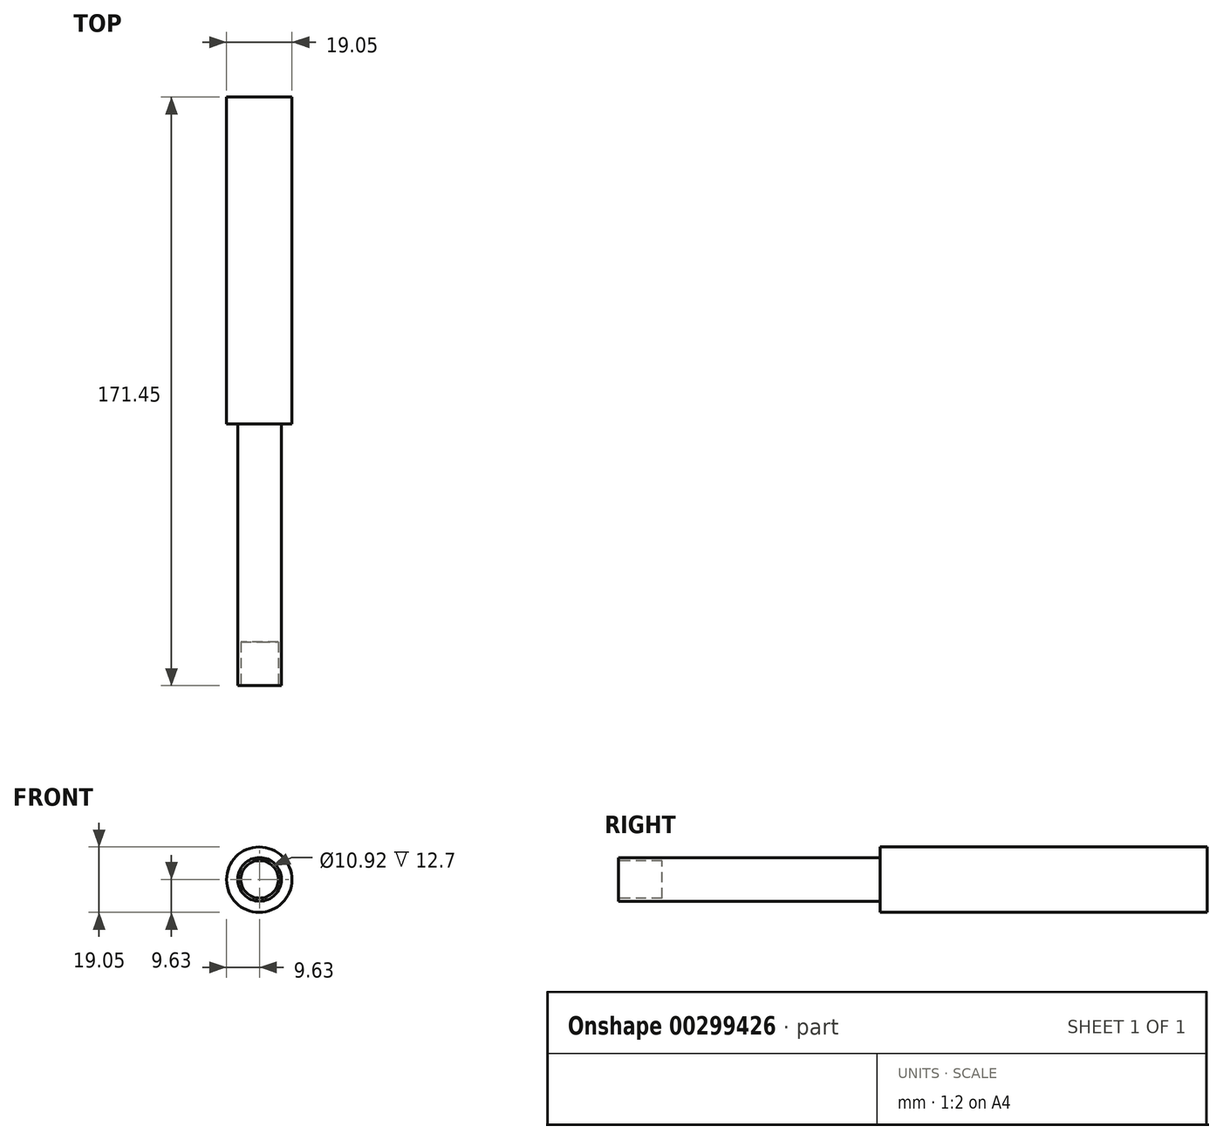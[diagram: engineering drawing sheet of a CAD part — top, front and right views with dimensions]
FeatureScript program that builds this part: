
annotation { "Feature Type Name" : "Feature", "Feature Type Description" : "" }
export const myFeature = defineFeature(function(context is Context, id is Id, definition is map)
    precondition{}
    {
        {
            var Q0;
            Q0=qCreatedBy(makeId("Front.planeOp"),FACE);
            var sketch = newSketch(context, id + "F0", { "sketchPlane" : qUnion([Q0])});
            skCircle(sketch, "E0", {"center": v(-0.1, -0.1) * mm, "radius": 9.53 * mm});
            skSolve(sketch);
        }
        {
            var Q0;
            Q0=makeQuery(id+"F0.imprint","IMPRINT",FACE,{"disambiguationData":[TD([[makeQuery(id+"F0.imprint","IMPRINT",EDGE,{"derivedFrom":sQuery(id+"F0.wireOp",EDGE,"E0")}),1.0]])]});
            extrude(context, id + "F1", {"entities" : qUnion([Q0]), "oppositeDirection" : true, "depth" : 95.25 * mm});
        }
        {
            var Q0;
            Q0=makeQuery(id+"F1.opExtrude","CAP_FACE",FACE,{"disambiguationData":[OSD([sQuery(id+"F0.wireOp",EDGE,"E0")])],"isStart":true});
            var sketch = newSketch(context, id + "F2", { "sketchPlane" : qUnion([Q0])});
            skCircle(sketch, "E1", {"center": v(0, 0) * mm, "radius": 6.35 * mm});
            skSolve(sketch);
        }
        {
            var Q0;
            Q0 = qSketchRegion(id + "F2", true);
            extrude(context, id + "F3", {"entities" : qUnion([Q0]), "operationType" : NewBodyOperationType.ADD, "depth" : 76.2 * mm});
        }
        {
            var Q0;
            Q0=makeQuery(id+"F3.opExtrude","CAP_FACE",FACE,{"disambiguationData":[OSD([sQuery(id+"F2.wireOp",EDGE,"E1")])],"isStart":false});
            var sketch = newSketch(context, id + "F4", { "sketchPlane" : qUnion([Q0])});
            skCircle(sketch, "E2", {"center": v(0, 0) * mm, "radius": 5.46 * mm});
            skSolve(sketch);
        }
        {
            var Q0;
            Q0=makeQuery(id+"F4.imprint","IMPRINT",FACE,{"disambiguationData":[TD([[makeQuery(id+"F4.imprint","IMPRINT",EDGE,{"derivedFrom":sQuery(id+"F4.wireOp",EDGE,"E2")}),1.0]])]});
            extrude(context, id + "F5", {"entities" : qUnion([Q0]), "operationType" : NewBodyOperationType.REMOVE, "oppositeDirection" : true, "depth" : 12.7 * mm});
        }
    });
